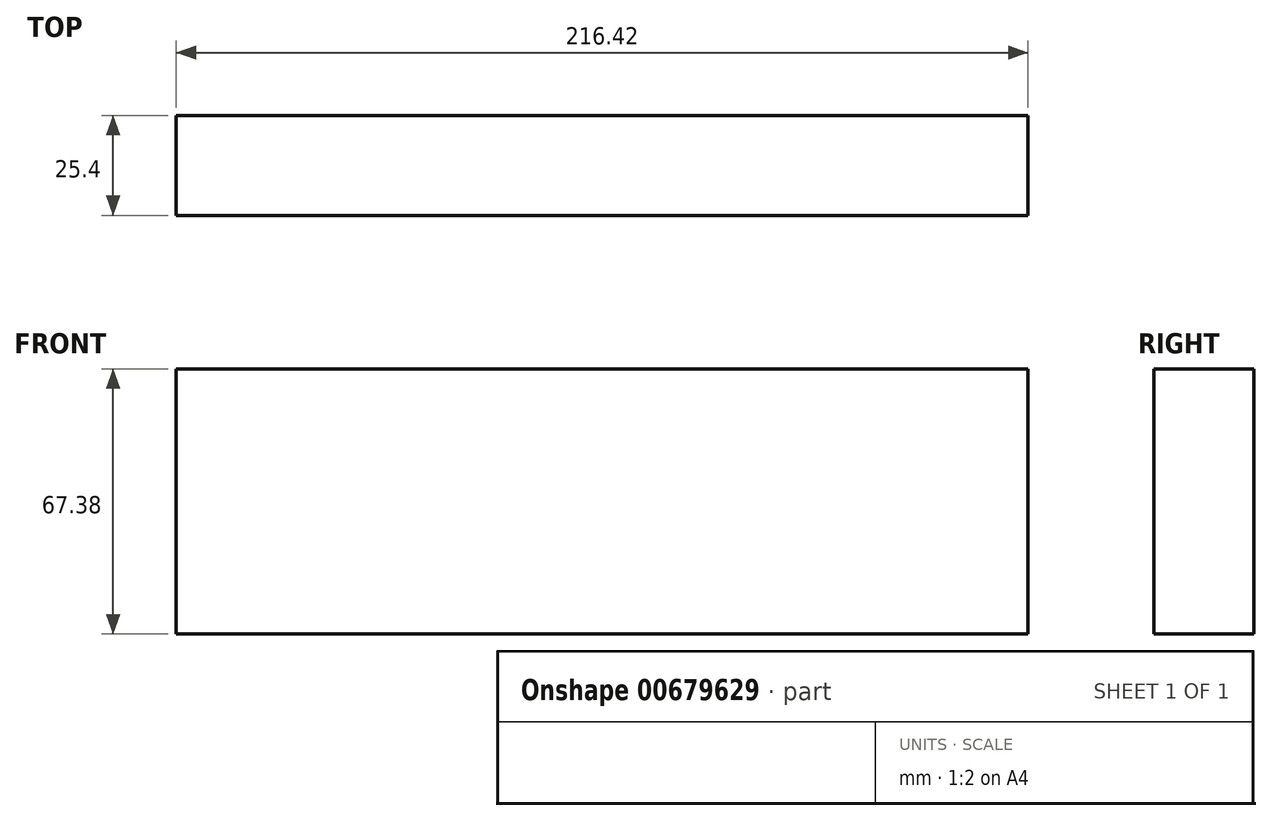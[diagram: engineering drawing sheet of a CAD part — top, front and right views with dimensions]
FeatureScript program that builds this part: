
annotation { "Feature Type Name" : "Feature", "Feature Type Description" : "" }
export const myFeature = defineFeature(function(context is Context, id is Id, definition is map)
    precondition{}
    {
        {
            var Q0;
            Q0=qCreatedBy(makeId("Front.planeOp"),FACE);
            var sketch = newSketch(context, id + "F0", { "sketchPlane" : qUnion([Q0])});
            skLineSegment(sketch, "E0.bottom", {"start": v(-113.35, 47.9) * mm, "end": v(103.07, 47.9) * mm});
            skLineSegment(sketch, "E0.top", {"start": v(-113.35, -19.48) * mm, "end": v(103.07, -19.48) * mm});
            skLineSegment(sketch, "E0.left", {"start": v(-113.35, 47.9) * mm, "end": v(-113.35, -19.48) * mm});
            skLineSegment(sketch, "E0.right", {"start": v(103.07, 47.9) * mm, "end": v(103.07, -19.48) * mm});
            skSolve(sketch);
        }
        {
            var Q0;
            Q0=makeQuery(id+"F0.imprint","IMPRINT",FACE,{"disambiguationData":[TD([[makeQuery(id+"F0.imprint","IMPRINT",EDGE,{"derivedFrom":sQuery(id+"F0.wireOp",EDGE,"E0.bottom")}),-1.0]])]});
            extrude(context, id + "F1", {"entities" : qUnion([Q0]), "oppositeDirection" : true, "depth" : 25.4 * mm, "offsetDistance" : 25.4 * mm});
        }
    });
